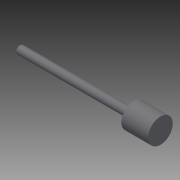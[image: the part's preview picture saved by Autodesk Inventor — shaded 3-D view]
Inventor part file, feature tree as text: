
AUTODESK INVENTOR PART (.ipt)
format: ipt  version: 2014 (Build 180170000, 170)  size: 116,736 bytes
history: native  units: in
note: dims shown in document units (in); Inventor stores cm internally (conversion verified against a paired STEP export)
features: other x49, revolve x2, sketch x2
ambient origin geometry x8: Origin, YZ Plane, XZ Plane, XY Plane, X Axis, Y Axis, Z Axis, Center Point
bodies: Solid1 (feature_tree)
feature tree (53):
  revolve  "Revolution1"  Angle=360.0deg
  revolve  "Revolution2"  [1 undecoded]
  other  "h1_XY"
  other  "h1_YZ"
  other  "h1_ZX"
  other  "h1_X"
  other  "h1_Y"
  other  "h1_Z"
  other  "h1_Center"
  other  "h2_XY"
  other  "h2_YZ"
  other  "h2_ZX"
  other  "h2_X"
  other  "h2_Y"
  other  "h2_Z"
  other  "h2_Center"
  other  "k1_XY"
  other  "k1_YZ"
  other  "k1_ZX"
  other  "k1_X"
  other  "k1_Y"
  other  "k1_Z"
  other  "k1_Center"
  other  "k2_XY"
  other  "k2_YZ"
  other  "k2_ZX"
  other  "k2_X"
  other  "k2_Y"
  other  "k2_Z"
  other  "k2_Center"
  other  "start_XY"
  other  "start_YZ"
  other  "start_ZX"
  other  "start_X"
  other  "start_Y"
  other  "start_Z"
  other  "start_Center"
  other  "to_prc_XY"
  other  "to_prc_YZ"
  other  "to_prc_ZX"
  other  "to_prc_X"
  other  "to_prc_Y"
  other  "to_prc_Z"
  other  "to_prc_Center"
  other  "to_rod_guide_XY"
  other  "to_rod_guide_YZ"
  other  "to_rod_guide_ZX"
  other  "to_rod_guide_X"
  other  "to_rod_guide_Y"
  other  "to_rod_guide_Z"
  other  "to_rod_guide_Center"
  sketch  "Sketch_5"  dims[d0=360.0deg d1=360.0deg]
  sketch  "Sketch_14"
note: 1 required parameter value undecoded (feature->parameter linkage not recoverable at this tier; creation-order binding heuristic only, values carry confidence <= 0.55)
